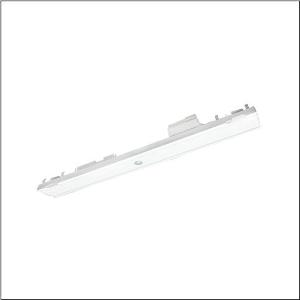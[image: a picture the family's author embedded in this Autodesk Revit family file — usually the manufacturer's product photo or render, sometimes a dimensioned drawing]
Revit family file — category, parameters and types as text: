
# Revit family: licross_r_56tl117c4x31_6d2f
name_source: partatom
category: Lighting Fixtures
units: mm (PartAtom-declared; Revit-internal decimal feet)

## family parameters
Cut with Voids When Loaded = No
Host = Face
Light Source = No
Part Type = Normal
Room Calculation Point = No
Round Connector Dimension = Use Diameter
Shared = No

## types (1)
- Licross® (1 x LED, 310 lm, 3.9 W, 4000K)
    Apparent Load = 4 VA
    CIE Flux Codes = 84 95 98 100 100
    Color Rendering = 70
    Color Temperature = 4000K
    Default Elevation = 1800 mm
    Description = Licross®, luminaire insert, of sheet steel, coil coated, white, length: 500mm, width: 59mm, height: 60mm, mounting height: 7..17m, emergency light element,LED rated luminous flux: 310lm, light colour: 740, control gear: CEAG, with plug, 6-pole, with phase selection, mains connection: 220..240V, AC/DC, 0/50..60Hz, rated input power: 3.9W, halogen-free wiring, for trunking rail, 9..14-pole, for emergency light function, supply monitoring module CEAG, with address switch, choice between two emergency light lines via tool-free moving of contact pin prior to installation in trunking rail, primary light control with lens, of PMMA, primary optical cover: cover, of PMMA, light emission: direct distribution, primary light characteristic: symmetric,  for area, compatible with all CEAG STAR technology systems (ZB-S, DG-S (DualGuard-S), LP-STAR, AT-S+), protection rating (complete): IP40, insulation class (complete): insulation class I (protective earthing), certification: CE, UKCA, protection symbol: D if used in an environment without relevant dust loads, impact resistance: IK06, permissible ambient temperature for indoor applications: -20..+40°C, packaging unit: 1 piece
    Height = 60 mm  [stored 0.19685 ft]
    Lamp = 1 x LED
    Lamp Light Flux = 310 lm
    Lamp Power = 3.9 W
    Lamp count = 1
    Length = 500 mm  [stored 1.64042 ft]
    Luminous efficacy = 79 lm/W
    Manufacturer = Siteco
    ModVariant = No
    Model = 56TL117C4X31
    Mounting Place = Ceiling
    Mounting Type = Pendant
    Number of Poles = 1
    OnlyDefault = Yes
    Power Factor = 1
    Product Name = Licross®
    Product group = luminaire insert
    ProductGroupID = 901
    Protection Class = Protection class I
    Protection Degree = IP 40
    RLX_Detail_Level = 1
    RLX_Emergency_Light_Flux = 0 lm
    RLX_Emergency_Type = 0
    RLX_Emergency_Type_DB = No
    RlxData = <blob elided: 17797 chars, md5=413be567>
    Socket = socket
    Standby Power = 0 W
    System Light Flux = 310 lm
    System Power = 4 W
    Type Comments = Product without accessories
    Type Image = l_1251804.jpg
    URL = http://relux.com
    VarID = ---
    Voltage = 0 V
    Weight = 0.00 kg
    Width = 59 mm

note: [stored X ft] marks values corroborated as IEEE doubles in the binary element streams (Revit-internal decimal feet)

## geometry (parser evidence)
native form markers: Blend x4, Sweep x12
no freeform markers — native parametric forms only
